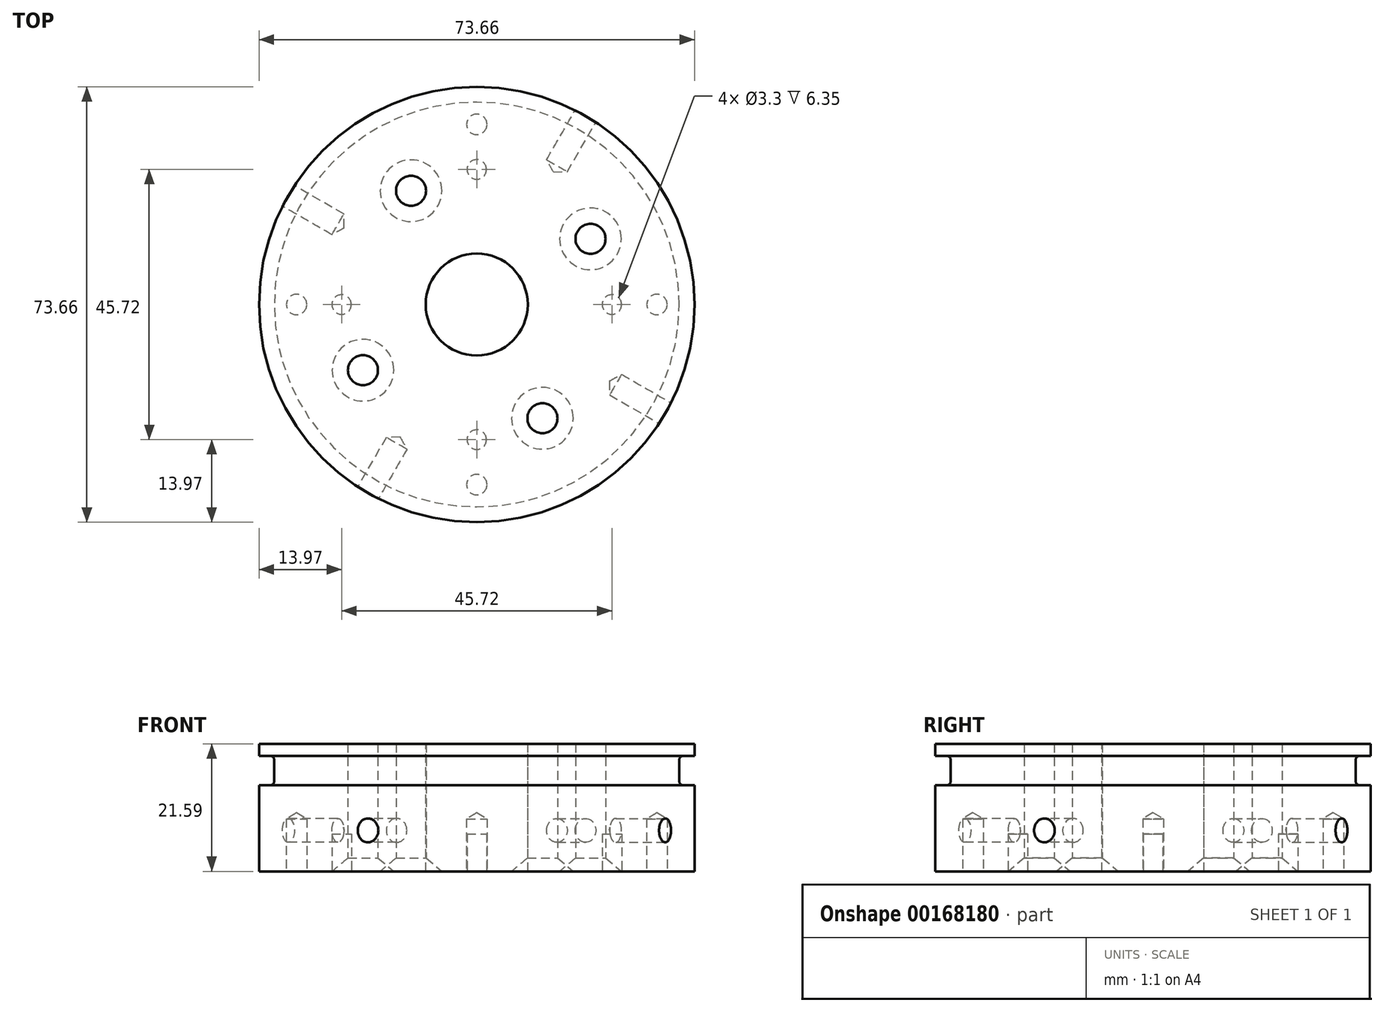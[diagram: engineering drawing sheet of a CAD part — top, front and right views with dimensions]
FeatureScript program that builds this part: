
annotation { "Feature Type Name" : "Feature", "Feature Type Description" : "" }
export const myFeature = defineFeature(function(context is Context, id is Id, definition is map)
    precondition{}
    {
        {
            var Q0;
            Q0=qCreatedBy(makeId("Top.planeOp"),FACE);
            var sketch = newSketch(context, id + "F0", { "sketchPlane" : qUnion([Q0])});
            skCircle(sketch, "E0", {"center": v(0, 0) * mm, "radius": 36.83 * mm});
            skSolve(sketch);
        }
        {
            var Q0;
            Q0=makeQuery(id+"F0.imprint","IMPRINT",FACE,{"disambiguationData":[TD([[makeQuery(id+"F0.imprint","IMPRINT",EDGE,{"derivedFrom":sQuery(id+"F0.wireOp",EDGE,"E0")}),1.0]])]});
            extrude(context, id + "F1", {"entities" : qUnion([Q0]), "depth" : 21.59 * mm});
        }
        {
            var Q0;
            Q0=makeQuery(id+"FNZgXB3MDCEPfWC_1.boolean.opBoolean","SPLIT",FACE,{"disambiguationData":[TD([makeQuery(id+"FNZgXB3MDCEPfWC_1.opExtrude","SWEPT_FACE",FACE,{"disambiguationData":[OSD([sQuery(id+"FiLk9hSRQ8Dv81E_1.wireOp",EDGE,"Xvq2NHEn-EDZK-GzOR-rNrk-moL4fFsD4KvI")])]})])],"derivedFrom":makeQuery(id+"F1.opExtrude","CAP_FACE",FACE,{"disambiguationData":[OSD([sQuery(id+"F0.wireOp",EDGE,"E0")])],"isStart":false})});
            var sketch = newSketch(context, id + "F2", { "sketchPlane" : qUnion([Q0])});
            skCircle(sketch, "E1", {"center": v(0, 0) * mm, "radius": 8.64 * mm});
            skSolve(sketch);
        }
        {
            var Q0;
            Q0=qSketchRegion(id+"F2",true);
            extrude(context, id + "F3", {"entities" : qUnion([Q0]), "operationType" : NewBodyOperationType.REMOVE, "endBound" : BoundingType.THROUGH_ALL, "oppositeDirection" : true, "depth" : 25.4 * mm});
        }
        {
            var Q0;
            Q0=makeQuery(id+"FOQC5dfjhO448EJ_1.boolean.opBoolean","SPLIT",FACE,{"disambiguationData":[TD([makeQuery(id+"F3.boolean.opBoolean","COPY",FACE,{"derivedFrom":makeQuery(id+"F3.opExtrude","SWEPT_FACE",FACE,{"disambiguationData":[OSD([sQuery(id+"F2.wireOp",EDGE,"E1")])]})})])],"derivedFrom":makeQuery(id+"F1.opExtrude","CAP_FACE",FACE,{"disambiguationData":[OSD([sQuery(id+"F0.wireOp",EDGE,"E0")])],"isStart":false})});
            cPlane(context, id + "F4", {"entities" : qUnion([Q0]), "cplaneType" : CPlaneType.OFFSET, "offset" : 2.03 * mm, "oppositeDirection" : true, "width" : 152.4 * mm, "height" : 152.4 * mm});
        }
        {
            var Q0;
            Q0=qCreatedBy(id+"F4.planeOp",FACE);
            var sketch = newSketch(context, id + "F5", { "sketchPlane" : qUnion([Q0])});
            skCircle(sketch, "E2", {"center": v(0, 0) * mm, "radius": 34.24 * mm});
            skCircle(sketch, "E3.0", {"center": v(0, 0) * mm, "radius": 36.83 * mm});
            skSolve(sketch);
        }
        {
            var Q0;
            Q0=qSketchRegion(id+"F5",true);
            extrude(context, id + "F6", {"entities" : qUnion([Q0]), "operationType" : NewBodyOperationType.REMOVE, "oppositeDirection" : true, "depth" : 5 * mm});
        }
        {
            var Q0;
            Q0=makeQuery(id+"F6.boolean.opBoolean","COPY",EDGE,{"derivedFrom":makeQuery(id+"F6.opExtrude","CAP_EDGE",EDGE,{"disambiguationData":[OSD([sQuery(id+"F5.wireOp",EDGE,"E2")])],"isStart":false})});
            var Q1;
            Q1=makeQuery(id+"F6.boolean.opBoolean","COPY",EDGE,{"derivedFrom":makeQuery(id+"F6.opExtrude","CAP_EDGE",EDGE,{"disambiguationData":[OSD([sQuery(id+"F5.wireOp",EDGE,"E2")])],"isStart":true})});
            fillet(context, id + "F7", {"entities" : qUnion([Q0, Q1]), "radius" : 0.76 * mm, "tangentPropagation" : true, "allowEdgeOverflow" : false});
        }
        {
            var Q0;
            {var subQ1=sQuery(id+"F0.wireOp",EDGE,"E0");var subQ2=makeQuery(id+"F1.opExtrude","SWEPT_FACE",FACE,{"disambiguationData":[OSD([subQ1])]});Q0=makeQuery(id+"FkcieFRIapZdHPD_1.boolean.opBoolean","SPLIT",FACE,{"disambiguationData":[TD([subQ2])],"derivedFrom":makeQuery(id+"F1.opExtrude","CAP_FACE",FACE,{"disambiguationData":[OSD([subQ1])],"isStart":false})});}
            var sketch = newSketch(context, id + "F8", { "sketchPlane" : qUnion([Q0])});
            skCircle(sketch, "E4.0", {"center": v(0, 0) * mm, "radius": 36.83 * mm, "construction": true});
            skPoint(sketch, "E5", {"position": v(-18.41, -31.9) * mm});
            skLineSegment(sketch, "E6", {"start": v(0, -36.83) * mm, "end": v(0, 0) * mm, "construction": true});
            skLineSegment(sketch, "E7", {"start": v(0, 0) * mm, "end": v(-17.96, -31.1) * mm, "construction": true});
            skLineSegment(sketch, "E8", {"start": v(-17.96, -31.1) * mm, "end": v(-18.41, -31.9) * mm, "construction": true});
            skLineSegment(sketch, "E9", {"start": v(0, 0) * mm, "end": v(18.41, 31.9) * mm, "construction": true});
            skLineSegment(sketch, "E10", {"start": v(18.41, 31.9) * mm, "end": v(0, 0) * mm, "construction": true});
            skLineSegment(sketch, "E11", {"start": v(31.9, -18.41) * mm, "end": v(0, 0) * mm, "construction": true});
            skLineSegment(sketch, "E12", {"start": v(0, 0) * mm, "end": v(-31.9, 18.41) * mm, "construction": true});
            skPoint(sketch, "E13", {"position": v(18.41, 31.9) * mm});
            skPoint(sketch, "E14", {"position": v(31.9, -18.41) * mm});
            skPoint(sketch, "E15", {"position": v(-31.9, 18.41) * mm});
            skSolve(sketch);
        }
        {
            var Q0;
            Q0=qCreatedBy(makeId("Front.planeOp"),FACE);
            var sketch = newSketch(context, id + "F9", { "sketchPlane" : qUnion([Q0])});
            skLineSegment(sketch, "E16", {"start": v(0, 0) * mm, "end": v(0, 38.57) * mm, "construction": true});
            skSolve(sketch);
        }
        {
            var Q0;
            Q0=sQuery(id+"F9.wireOp",EDGE,"E16");
            cPlane(context, id + "F10", {"entities" : qUnion([Q0]), "cplaneType" : CPlaneType.LINE_ANGLE, "offset" : 25.4 * mm, "angle" : 60 * degree, "width" : 152.4 * mm, "height" : 152.4 * mm});
        }
        {
            var Q0;
            Q0=sQuery(id+"F8.wireOp",VERTEX,"E5");
            var Q1;
            Q1=qCreatedBy(id+"F10.planeOp",FACE);
            cPlane(context, id + "F11", {"entities" : qUnion([Q0, Q1]), "cplaneType" : CPlaneType.PLANE_POINT, "offset" : 25.4 * mm, "width" : 152.4 * mm, "height" : 152.4 * mm});
        }
        {
            var Q0;
            Q0=qCreatedBy(id+"F11.planeOp",FACE);
            var Q1;
            Q1=sQuery(id+"F8.wireOp",VERTEX,"E13");
            cPlane(context, id + "F12", {"entities" : qUnion([Q0, Q1]), "cplaneType" : CPlaneType.PLANE_POINT, "offset" : 25.4 * mm, "width" : 152.4 * mm, "height" : 152.4 * mm});
        }
        {
            var Q0;
            Q0=sQuery(id+"F9.wireOp",EDGE,"E16");
            cPlane(context, id + "F13", {"entities" : qUnion([Q0]), "cplaneType" : CPlaneType.LINE_ANGLE, "offset" : 25.4 * mm, "angle" : 150 * degree, "width" : 152.4 * mm, "height" : 152.4 * mm});
        }
        {
            var Q0;
            Q0=sQuery(id+"F8.wireOp",VERTEX,"E15");
            var Q1;
            Q1=qCreatedBy(id+"F13.planeOp",FACE);
            cPlane(context, id + "F14", {"entities" : qUnion([Q0, Q1]), "cplaneType" : CPlaneType.PLANE_POINT, "offset" : 25.4 * mm, "width" : 152.4 * mm, "height" : 152.4 * mm});
        }
        {
            var Q0;
            Q0=qCreatedBy(id+"F13.planeOp",FACE);
            var Q1;
            Q1=sQuery(id+"F8.wireOp",VERTEX,"E14");
            cPlane(context, id + "F15", {"entities" : qUnion([Q0, Q1]), "cplaneType" : CPlaneType.PLANE_POINT, "offset" : 25.4 * mm, "width" : 152.4 * mm, "height" : 152.4 * mm});
        }
        {
            var Q0;
            Q0=qCreatedBy(id+"F11.planeOp",FACE);
            var sketch = newSketch(context, id + "F16", { "sketchPlane" : qUnion([Q0])});
            skLineSegment(sketch, "E17", {"start": v(0, 0) * mm, "end": v(0, 6.93) * mm, "construction": true});
            skPoint(sketch, "E18", {"position": v(0, 6.93) * mm});
            skSolve(sketch);
        }
        {
            var Q0;
            Q0=qCreatedBy(id+"F12.planeOp",FACE);
            var sketch = newSketch(context, id + "F17", { "sketchPlane" : qUnion([Q0])});
            skPoint(sketch, "E19", {"position": v(0, 6.93) * mm});
            skLineSegment(sketch, "E20.0", {"start": v(0, 0) * mm, "end": v(0, 6.93) * mm, "construction": true});
            skSolve(sketch);
        }
        {
            var Q0;
            Q0=qCreatedBy(id+"F14.planeOp",FACE);
            var sketch = newSketch(context, id + "F18", { "sketchPlane" : qUnion([Q0])});
            skLineSegment(sketch, "E21", {"start": v(0, 0) * mm, "end": v(0, 6.93) * mm, "construction": true});
            skLineSegment(sketch, "E22.0", {"start": v(-36.83, 0) * mm, "end": v(-36.83, 6.93) * mm, "construction": true});
            skPoint(sketch, "E23", {"position": v(0, 6.93) * mm});
            skLineSegment(sketch, "E24", {"start": v(-36.83, 6.93) * mm, "end": v(0, 6.93) * mm, "construction": true});
            skSolve(sketch);
        }
        {
            var Q0;
            Q0=qCreatedBy(id+"F15.planeOp",FACE);
            var sketch = newSketch(context, id + "F19", { "sketchPlane" : qUnion([Q0])});
            skLineSegment(sketch, "E25.0", {"start": v(0, 0) * mm, "end": v(0, 6.93) * mm, "construction": true});
            skPoint(sketch, "E26", {"position": v(0, 6.93) * mm});
            skSolve(sketch);
        }
        {
            var Q0;
            Q0=sQuery(id+"F19.wireOp",VERTEX,"E26");
            var Q1;
            Q1=makeQuery(id+"F1.opExtrude","SWEPT_BODY",BODY,{"disambiguationData":[OSD([sQuery(id+"F0.wireOp",EDGE,"E0")])]});
            hole(context, id + "F20", {"style" : HoleStyle.SIMPLE, "endStyle" : HoleEndStyle.BLIND, "oppositeDirection" : true, "standardTappedOrClearance" : lookupTablePath({ "standard" : "ANSI", "engagement" : "75%", "pitch" : "32 tpi", "size" : "#10", "type" : "Tapped" }), "standardBlindInLast" : lookupTablePath({ "standard" : "ANSI", "engagement" : "75%", "pitch" : "32 tpi", "size" : "#10", "type" : "Tapped" }), "holeDiameter" : 4.04 * mm, "holeDepth" : 9.65 * mm, "locations" : qUnion([Q0]), "scope" : qUnion([Q1]), "majorDiameter" : 4.83 * mm});
        }
        {
            var Q0;
            Q0=sQuery(id+"F18.wireOp",VERTEX,"E23");
            var Q1;
            Q1=makeQuery(id+"F1.opExtrude","SWEPT_BODY",BODY,{"disambiguationData":[OSD([sQuery(id+"F0.wireOp",EDGE,"E0")])]});
            hole(context, id + "F21", {"style" : HoleStyle.SIMPLE, "endStyle" : HoleEndStyle.BLIND, "standardTappedOrClearance" : lookupTablePath({ "standard" : "ANSI", "engagement" : "75%", "pitch" : "32 tpi", "size" : "#10", "type" : "Tapped" }), "standardBlindInLast" : lookupTablePath({ "standard" : "ANSI", "engagement" : "75%", "pitch" : "32 tpi", "size" : "#10", "type" : "Tapped" }), "holeDiameter" : 4.04 * mm, "holeDepth" : 9.65 * mm, "locations" : qUnion([Q0]), "scope" : qUnion([Q1]), "majorDiameter" : 4.83 * mm});
        }
        {
            var Q0;
            Q0=sQuery(id+"F16.wireOp",VERTEX,"E18");
            var Q1;
            Q1=makeQuery(id+"F1.opExtrude","SWEPT_BODY",BODY,{"disambiguationData":[OSD([sQuery(id+"F0.wireOp",EDGE,"E0")])]});
            hole(context, id + "F22", {"style" : HoleStyle.SIMPLE, "endStyle" : HoleEndStyle.BLIND, "oppositeDirection" : true, "standardTappedOrClearance" : lookupTablePath({ "standard" : "ANSI", "engagement" : "75%", "pitch" : "32 tpi", "size" : "#10", "type" : "Tapped" }), "standardBlindInLast" : lookupTablePath({ "standard" : "ANSI", "engagement" : "75%", "pitch" : "32 tpi", "size" : "#10", "type" : "Tapped" }), "holeDiameter" : 4.04 * mm, "holeDepth" : 9.65 * mm, "locations" : qUnion([Q0]), "scope" : qUnion([Q1]), "majorDiameter" : 4.83 * mm});
        }
        {
            var Q0;
            Q0=sQuery(id+"F17.wireOp",VERTEX,"E19");
            var Q1;
            Q1=makeQuery(id+"F1.opExtrude","SWEPT_BODY",BODY,{"disambiguationData":[OSD([sQuery(id+"F0.wireOp",EDGE,"E0")])]});
            hole(context, id + "F23", {"style" : HoleStyle.SIMPLE, "endStyle" : HoleEndStyle.BLIND, "standardTappedOrClearance" : lookupTablePath({ "standard" : "ANSI", "engagement" : "75%", "pitch" : "32 tpi", "size" : "#10", "type" : "Tapped" }), "standardBlindInLast" : lookupTablePath({ "standard" : "ANSI", "engagement" : "75%", "pitch" : "32 tpi", "size" : "#10", "type" : "Tapped" }), "holeDiameter" : 4.04 * mm, "holeDepth" : 9.65 * mm, "locations" : qUnion([Q0]), "scope" : qUnion([Q1]), "majorDiameter" : 4.83 * mm});
        }
        {
            var Q0;
            Q0=makeQuery(id+"F1.opExtrude","CAP_FACE",FACE,{"disambiguationData":[OSD([sQuery(id+"F0.wireOp",EDGE,"E0")])],"isStart":true});
            var sketch = newSketch(context, id + "F24", { "sketchPlane" : qUnion([Q0])});
            skLineSegment(sketch, "E27", {"start": v(0, 0) * mm, "end": v(-11.11, -19.25) * mm, "construction": true});
            skPoint(sketch, "E28", {"position": v(-11.11, -19.25) * mm});
            skPoint(sketch, "E29.1.0", {"position": v(19.25, -11.11) * mm});
            skPoint(sketch, "E29.2.0", {"position": v(11.11, 19.25) * mm});
            skPoint(sketch, "E29.3.0", {"position": v(-19.25, 11.11) * mm});
            skPoint(sketch, "E29.center", {"position": v(0, 0) * mm});
            skSolve(sketch);
        }
        {
            var Q0;
            Q0=sQuery(id+"F24.wireOp",VERTEX,"E29.3.0");
            var Q1;
            Q1=sQuery(id+"F24.wireOp",VERTEX,"E28");
            var Q2;
            Q2=sQuery(id+"F24.wireOp",VERTEX,"E29.1.0");
            var Q3;
            Q3=sQuery(id+"F24.wireOp",VERTEX,"E29.2.0");
            var Q4;
            Q4=makeQuery(id+"F1.opExtrude","SWEPT_BODY",BODY,{"disambiguationData":[OSD([sQuery(id+"F0.wireOp",EDGE,"E0")])]});
            hole(context, id + "F25", {"style" : HoleStyle.C_SINK, "endStyle" : HoleEndStyle.THROUGH, "holeDiameter" : 5.08 * mm, "cSinkDiameter" : 10.44 * mm, "cSinkAngle" : 100 * degree, "locations" : qUnion([Q0, Q1, Q2, Q3]), "scope" : qUnion([Q4]), "isTappedThrough" : true});
        }
        {
            var Q0;
            Q0=makeQuery(id+"F1.opExtrude","CAP_FACE",FACE,{"disambiguationData":[OSD([sQuery(id+"F0.wireOp",EDGE,"E0")])],"isStart":true});
            var sketch = newSketch(context, id + "F26", { "sketchPlane" : qUnion([Q0])});
            skPoint(sketch, "E30", {"position": v(-30.48, 0) * mm});
            skPoint(sketch, "E31.1.0", {"position": v(0, -30.48) * mm});
            skPoint(sketch, "E31.2.0", {"position": v(30.48, 0) * mm});
            skPoint(sketch, "E31.3.0", {"position": v(0, 30.48) * mm});
            skPoint(sketch, "E31.center", {"position": v(0, 0) * mm});
            skSolve(sketch);
        }
        {
            var Q0;
            Q0=sQuery(id+"F26.wireOp",VERTEX,"E30");
            var Q1;
            Q1=sQuery(id+"F26.wireOp",VERTEX,"E31.1.0");
            var Q2;
            Q2=sQuery(id+"F26.wireOp",VERTEX,"E31.3.0");
            var Q3;
            Q3=sQuery(id+"F26.wireOp",VERTEX,"E31.2.0");
            var Q4;
            Q4=makeQuery(id+"F1.opExtrude","SWEPT_BODY",BODY,{"disambiguationData":[OSD([sQuery(id+"F0.wireOp",EDGE,"E0")])]});
            hole(context, id + "F27", {"style" : HoleStyle.SIMPLE, "endStyle" : HoleEndStyle.BLIND, "standardTappedOrClearance" : lookupTablePath({ "standard" : "ANSI", "engagement" : "75%", "pitch" : "32 tpi", "size" : "#8", "type" : "Tapped" }), "standardBlindInLast" : lookupTablePath({ "standard" : "ANSI", "engagement" : "75%", "pitch" : "32 tpi", "size" : "#8", "type" : "Tapped" }), "holeDiameter" : 3.45 * mm, "holeDepth" : 8.9 * mm, "locations" : qUnion([Q0, Q1, Q2, Q3]), "scope" : qUnion([Q4]), "majorDiameter" : 4.17 * mm});
        }
        {
            var Q0;
            Q0=makeQuery(id+"F1.opExtrude","CAP_FACE",FACE,{"disambiguationData":[OSD([sQuery(id+"F0.wireOp",EDGE,"E0")])],"isStart":true});
            var sketch = newSketch(context, id + "F28", { "sketchPlane" : qUnion([Q0])});
            skCircle(sketch, "E32", {"center": v(-22.86, 0) * mm, "radius": 1.65 * mm});
            skCircle(sketch, "E33.1.0", {"center": v(0, -22.86) * mm, "radius": 1.65 * mm});
            skCircle(sketch, "E33.2.0", {"center": v(22.86, 0) * mm, "radius": 1.65 * mm});
            skCircle(sketch, "E33.3.0", {"center": v(0, 22.86) * mm, "radius": 1.65 * mm});
            skPoint(sketch, "E33.center", {"position": v(0, 0) * mm});
            skSolve(sketch);
        }
        {
            var Q0;
            Q0=qSketchRegion(id+"F28",true);
            extrude(context, id + "F29", {"entities" : qUnion([Q0]), "operationType" : NewBodyOperationType.REMOVE, "oppositeDirection" : true, "depth" : 6.35 * mm});
        }
    });
